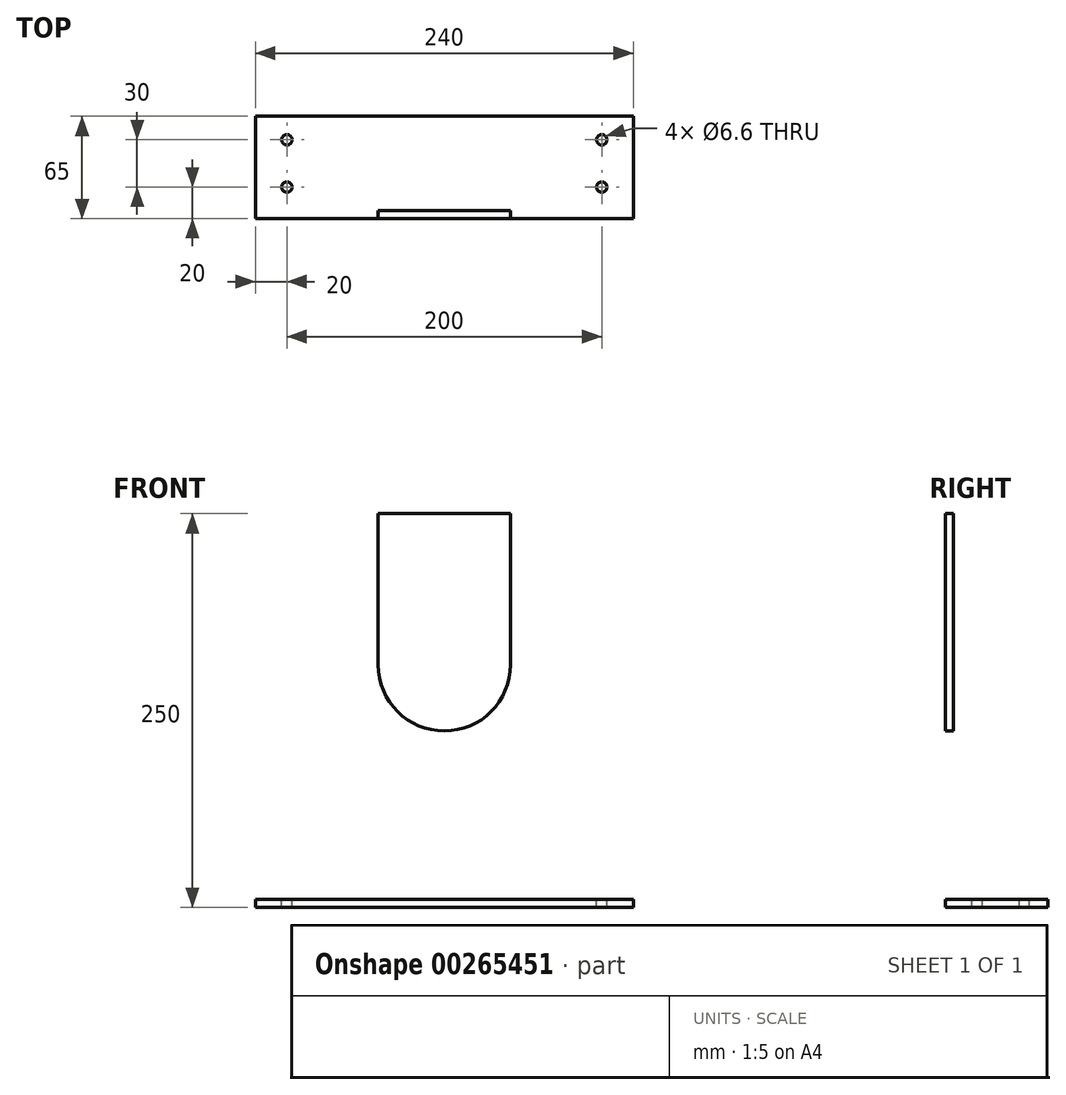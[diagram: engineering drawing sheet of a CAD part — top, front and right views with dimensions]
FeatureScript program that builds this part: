
annotation { "Feature Type Name" : "Feature", "Feature Type Description" : "" }
export const myFeature = defineFeature(function(context is Context, id is Id, definition is map)
    precondition{}
    {
        {
            var Q0;
            Q0=qCreatedBy(makeId("Right.planeOp"),FACE);
            var sketch = newSketch(context, id + "F0", { "sketchPlane" : qUnion([Q0])});
            skLineSegment(sketch, "E0.bottom", {"start": v(0, 250) * mm, "end": v(5, 250) * mm});
            skLineSegment(sketch, "E0.left", {"start": v(0, 250) * mm, "end": v(0, 0) * mm});
            skLineSegment(sketch, "E0.right", {"start": v(5, 250) * mm, "end": v(5, 5) * mm});
            skLineSegment(sketch, "E1.top", {"start": v(5, 5) * mm, "end": v(65, 5) * mm});
            skLineSegment(sketch, "E1.right", {"start": v(65, 0) * mm, "end": v(65, 5) * mm});
            skLineSegment(sketch, "E2", {"start": v(0, 0) * mm, "end": v(65, 0) * mm});
            skSolve(sketch);
        }
        {
            var Q0;
            Q0=makeQuery(id+"F0.imprint","IMPRINT",FACE,{"disambiguationData":[TD([[makeQuery(id+"F0.imprint","IMPRINT",EDGE,{"derivedFrom":sQuery(id+"F0.wireOp",EDGE,"E0.bottom")}),-1.0]])]});
            extrude(context, id + "F1", {"entities" : qUnion([Q0]), "endBound" : BoundingType.SYMMETRIC, "depth" : 240 * mm, "offsetDistance" : 25 * mm});
        }
        {
            var Q0;
            Q0=makeQuery(id+"F1.opExtrude","SWEPT_FACE",FACE,{"disambiguationData":[OSD([sQuery(id+"F0.wireOp",EDGE,"E0.right")])]});
            var sketch = newSketch(context, id + "F2", { "sketchPlane" : qUnion([Q0])});
            skArc(sketch, "E3", {"start": v(42, 154) * mm, "mid": v(0, 112) * mm, "end": v(-42, 154) * mm});
            skLineSegment(sketch, "E4", {"start": v(-42, 154) * mm, "end": v(42, 154) * mm, "construction": true});
            skLineSegment(sketch, "E5", {"start": v(-42, 154) * mm, "end": v(-42, 250) * mm});
            skLineSegment(sketch, "E6", {"start": v(-42, 250) * mm, "end": v(42, 250) * mm});
            skLineSegment(sketch, "E7", {"start": v(42, 250) * mm, "end": v(42, 154) * mm});
            skSolve(sketch);
        }
        {
            var Q0;
            Q0=makeQuery(id+"F2.imprint","IMPRINT",FACE,{"disambiguationData":[TD([[makeQuery(id+"F2.imprint","IMPRINT",EDGE,{"derivedFrom":sQuery(id+"F2.wireOp",EDGE,"E3")}),-1.0]])]});
            extrude(context, id + "F3", {"entities" : qUnion([Q0]), "operationType" : NewBodyOperationType.REMOVE, "endBound" : BoundingType.UP_TO_NEXT, "oppositeDirection" : true, "depth" : 25 * mm, "offsetDistance" : 25 * mm});
        }
        {
            var Q0;
            Q0=makeQuery(id+"F1.opExtrude","SWEPT_FACE",FACE,{"disambiguationData":[OSD([sQuery(id+"F0.wireOp",EDGE,"E1.top")])]});
            var sketch = newSketch(context, id + "F4", { "sketchPlane" : qUnion([Q0])});
            skLineSegment(sketch, "E8.bottom", {"start": v(-100, 20) * mm, "end": v(100, 20) * mm, "construction": true});
            skLineSegment(sketch, "E8.top", {"start": v(-100, 50) * mm, "end": v(100, 50) * mm, "construction": true});
            skLineSegment(sketch, "E8.left", {"start": v(-100, 20) * mm, "end": v(-100, 50) * mm, "construction": true});
            skLineSegment(sketch, "E8.right", {"start": v(100, 20) * mm, "end": v(100, 50) * mm, "construction": true});
            skLineSegment(sketch, "E9", {"start": v(-120, 35) * mm, "end": v(120, 35) * mm, "construction": true});
            skLineSegment(sketch, "E10", {"start": v(0, 5) * mm, "end": v(0, 65) * mm, "construction": true});
            skSolve(sketch);
        }
        {
            var Q0;
            Q0=sQuery(id+"F4.wireOp",VERTEX,"E8.left.start");
            var Q1;
            Q1=sQuery(id+"F4.wireOp",VERTEX,"E8.left.end");
            var Q2;
            Q2=sQuery(id+"F4.wireOp",VERTEX,"E8.right.start");
            var Q3;
            Q3=sQuery(id+"F4.wireOp",VERTEX,"E8.top.end");
            var Q4;
            Q4=makeQuery(id+"F1.opExtrude","SWEPT_BODY",BODY,{"disambiguationData":[OSD([sQuery(id+"F0.wireOp",EDGE,"E0.bottom"),sQuery(id+"F0.wireOp",EDGE,"E0.left"),sQuery(id+"F0.wireOp",EDGE,"E0.right"),sQuery(id+"F0.wireOp",EDGE,"E1.top"),sQuery(id+"F0.wireOp",EDGE,"E1.right"),sQuery(id+"F0.wireOp",EDGE,"E2")])]});
            hole(context, id + "F5", {"style" : HoleStyle.SIMPLE, "endStyle" : HoleEndStyle.BLIND, "standardTappedOrClearance" : lookupTablePath({ "standard" : "ISO", "fit" : "Normal", "size" : "M6", "type" : "Clearance" }), "standardBlindInLast" : lookupTablePath({ "fit" : "Standard", "standard" : "ISO", "size" : "M6", "type" : "Clearance" }), "holeDiameter" : 6.6 * mm, "holeDepth" : 14.4 * mm, "tappedDepth" : 12 * mm, "tapClearance" : 3, "startFromSketch" : true, "locations" : qUnion([Q0, Q1, Q2, Q3]), "scope" : qUnion([Q4])});
        }
    });
